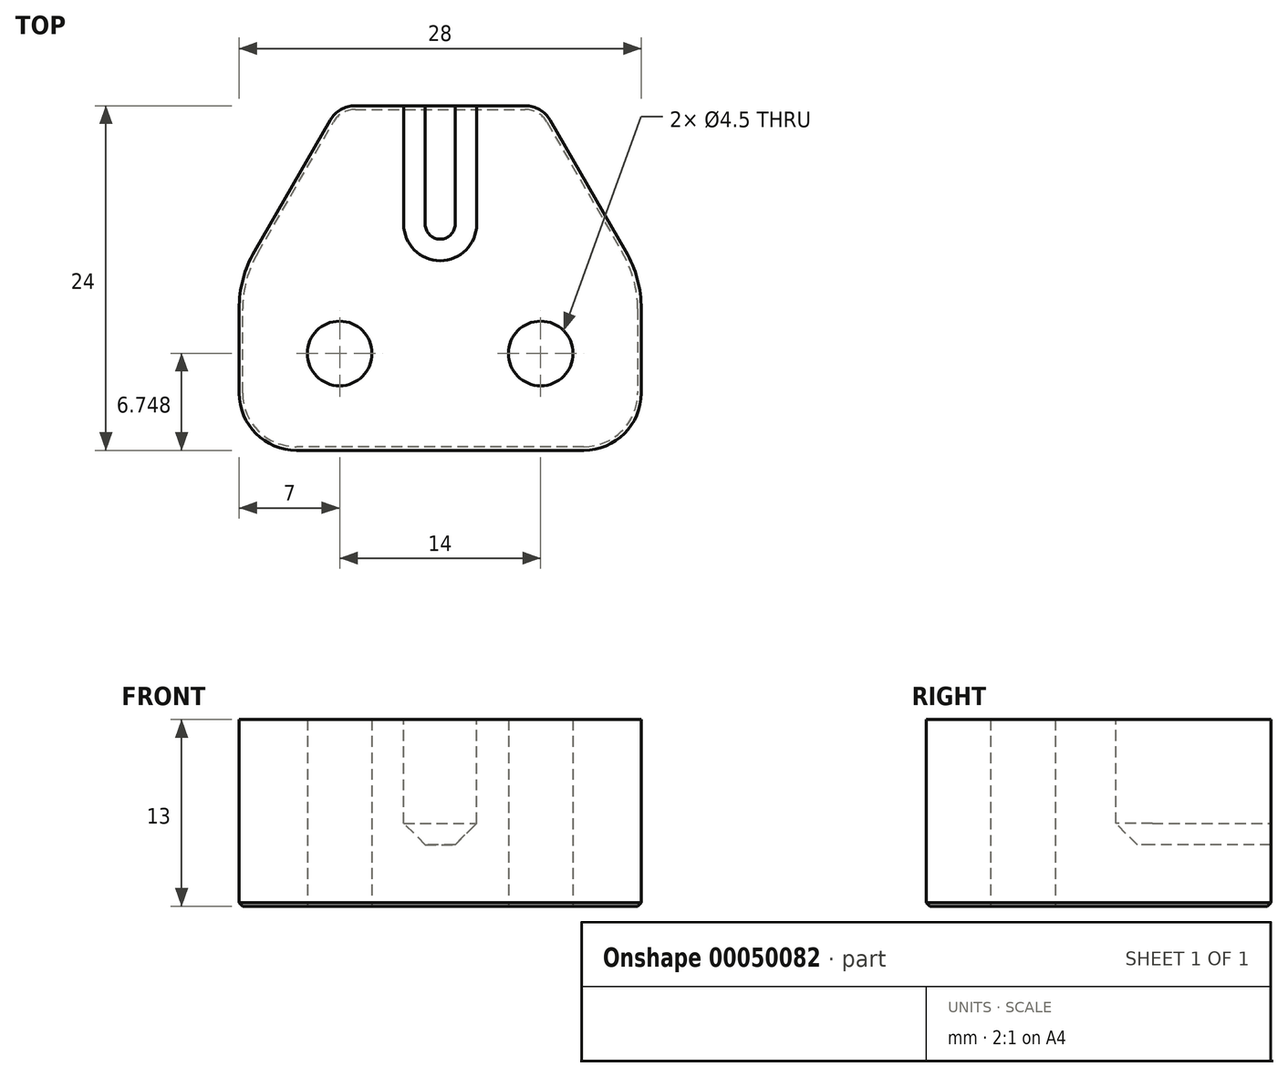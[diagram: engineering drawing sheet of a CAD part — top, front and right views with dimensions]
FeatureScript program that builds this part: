
annotation { "Feature Type Name" : "Feature", "Feature Type Description" : "" }
export const myFeature = defineFeature(function(context is Context, id is Id, definition is map)
    precondition{}
    {
        {
            var Q0;
            Q0=qCreatedBy(makeId("Top.planeOp"),FACE);
            var sketch = newSketch(context, id + "F0", { "sketchPlane" : qUnion([Q0])});
            skLineSegment(sketch, "E0", {"start": v(14, 2.75) * mm, "end": v(14, 14.75) * mm});
            skLineSegment(sketch, "E1", {"start": v(14, 14.75) * mm, "end": v(7.07, 26.75) * mm});
            skLineSegment(sketch, "E2", {"start": v(7.07, 26.75) * mm, "end": v(0, 26.75) * mm});
            skLineSegment(sketch, "E3", {"start": v(14, 2.75) * mm, "end": v(0, 2.75) * mm});
            skLineSegment(sketch, "E4.MirrorCS", {"start": v(-14, 2.75) * mm, "end": v(0, 2.75) * mm});
            skLineSegment(sketch, "E5.MirrorCS", {"start": v(-14, 2.75) * mm, "end": v(-14, 14.75) * mm});
            skLineSegment(sketch, "E6.MirrorCS", {"start": v(-7.07, 26.75) * mm, "end": v(0, 26.75) * mm});
            skLineSegment(sketch, "E7.MirrorCS", {"start": v(-14, 14.75) * mm, "end": v(-7.07, 26.75) * mm});
            skSolve(sketch);
        }
        {
            var Q0;
            Q0 = qSketchRegion(id + "F0", true);
            extrude(context, id + "F1", {"entities" : qUnion([Q0]), "depth" : 13 * mm});
        }
        {
            var Q0;
            Q0=makeQuery(id+"F1.opExtrude","SWEPT_EDGE",EDGE,{"disambiguationData":[OSD([sQuery(id+"F0.wireOp",EDGE,"E5.MirrorCS"),sQuery(id+"F0.wireOp",EDGE,"E7.MirrorCS")])]});
            var Q1;
            Q1=makeQuery(id+"F1.opExtrude","SWEPT_EDGE",EDGE,{"disambiguationData":[OSD([sQuery(id+"F0.wireOp",EDGE,"E0"),sQuery(id+"F0.wireOp",EDGE,"E1")])]});
            fillet(context, id + "F2", {"entities" : qUnion([Q0, Q1]), "radius" : 8 * mm, "tangentPropagation" : true, "allowEdgeOverflow" : false});
        }
        {
            var Q0;
            Q0=makeQuery(id+"F1.opExtrude","SWEPT_EDGE",EDGE,{"disambiguationData":[OSD([sQuery(id+"F0.wireOp",EDGE,"E6.MirrorCS"),sQuery(id+"F0.wireOp",EDGE,"E7.MirrorCS")])]});
            var Q1;
            Q1=makeQuery(id+"F1.opExtrude","SWEPT_EDGE",EDGE,{"disambiguationData":[OSD([sQuery(id+"F0.wireOp",EDGE,"E1"),sQuery(id+"F0.wireOp",EDGE,"E2")])]});
            fillet(context, id + "F3", {"entities" : qUnion([Q0, Q1]), "radius" : 2 * mm, "tangentPropagation" : true, "allowEdgeOverflow" : false});
        }
        {
            var Q0;
            Q0=makeQuery(id+"F1.opExtrude","CAP_FACE",FACE,{"disambiguationData":[OSD([sQuery(id+"F0.wireOp",EDGE,"E0"),sQuery(id+"F0.wireOp",EDGE,"E1"),sQuery(id+"F0.wireOp",EDGE,"E2"),sQuery(id+"F0.wireOp",EDGE,"E3"),sQuery(id+"F0.wireOp",EDGE,"E4.MirrorCS"),sQuery(id+"F0.wireOp",EDGE,"E5.MirrorCS"),sQuery(id+"F0.wireOp",EDGE,"E6.MirrorCS"),sQuery(id+"F0.wireOp",EDGE,"E7.MirrorCS")])],"isStart":false});
            var sketch = newSketch(context, id + "F4", { "sketchPlane" : qUnion([Q0])});
            skArc(sketch, "E8", {"start": v(-2.54, 18.5) * mm, "mid": v(0, 15.96) * mm, "end": v(2.54, 18.5) * mm});
            skLineSegment(sketch, "E9", {"start": v(-2.54, 18.5) * mm, "end": v(-2.54, 26.75) * mm});
            skLineSegment(sketch, "E10", {"start": v(2.54, 18.5) * mm, "end": v(2.54, 26.75) * mm});
            skLineSegment(sketch, "E11", {"start": v(2.54, 26.75) * mm, "end": v(-2.54, 26.75) * mm});
            skSolve(sketch);
        }
        {
            var Q0;
            Q0 = qSketchRegion(id + "F4", true);
            extrude(context, id + "F5", {"entities" : qUnion([Q0]), "operationType" : NewBodyOperationType.REMOVE, "oppositeDirection" : true, "depth" : (11 / 32 * 25.4) * mm, "offsetDistance" : 25 * mm});
        }
        {
            var Q0;
            Q0=makeQuery(id+"F1.opExtrude","CAP_FACE",FACE,{"disambiguationData":[OSD([sQuery(id+"F0.wireOp",EDGE,"E0"),sQuery(id+"F0.wireOp",EDGE,"E1"),sQuery(id+"F0.wireOp",EDGE,"E2"),sQuery(id+"F0.wireOp",EDGE,"E3"),sQuery(id+"F0.wireOp",EDGE,"E4.MirrorCS"),sQuery(id+"F0.wireOp",EDGE,"E5.MirrorCS"),sQuery(id+"F0.wireOp",EDGE,"E6.MirrorCS"),sQuery(id+"F0.wireOp",EDGE,"E7.MirrorCS")])],"isStart":true});
            var sketch = newSketch(context, id + "F6", { "sketchPlane" : qUnion([Q0])});
            skCircle(sketch, "E12", {"center": v(-7, -9.5) * mm, "radius": 2.25 * mm});
            skCircle(sketch, "E13.MirrorC", {"center": v(7, -9.5) * mm, "radius": 2.25 * mm});
            skSolve(sketch);
        }
        {
            var Q0;
            Q0 = qSketchRegion(id + "F6", true);
            extrude(context, id + "F7", {"entities" : qUnion([Q0]), "operationType" : NewBodyOperationType.REMOVE, "endBound" : BoundingType.THROUGH_ALL, "oppositeDirection" : true, "depth" : 25 * mm});
        }
        {
            var Q0;
            Q0=makeQuery(id+"F1.opExtrude","SWEPT_EDGE",EDGE,{"disambiguationData":[OSD([sQuery(id+"F0.wireOp",EDGE,"E4.MirrorCS"),sQuery(id+"F0.wireOp",EDGE,"E5.MirrorCS")])]});
            var Q1;
            Q1=makeQuery(id+"F1.opExtrude","SWEPT_EDGE",EDGE,{"disambiguationData":[OSD([sQuery(id+"F0.wireOp",EDGE,"E0"),sQuery(id+"F0.wireOp",EDGE,"E3")])]});
            fillet(context, id + "F8", {"entities" : qUnion([Q0, Q1]), "radius" : 4 * mm, "tangentPropagation" : true, "allowEdgeOverflow" : false});
        }
        {
            var Q0;
            Q0=makeQuery(id+"F5.boolean.opBoolean","COPY",EDGE,{"derivedFrom":makeQuery(id+"F5.opExtrude","CAP_EDGE",EDGE,{"disambiguationData":[OSD([sQuery(id+"F4.wireOp",EDGE,"E8")])],"isStart":false})});
            chamfer(context, id + "F9", {"entities" : qUnion([Q0]), "width" : 1.5 * mm, "tangentPropagation" : true});
        }
        {
            var Q0;
            Q0=makeQuery(id+"F7.boolean.opBoolean","COPY",EDGE,{"derivedFrom":makeQuery(id+"F7.opExtrude","CAP_EDGE",EDGE,{"disambiguationData":[OSD([sQuery(id+"F6.wireOp",EDGE,"E13.MirrorC")])],"isStart":true})});
            var Q1;
            Q1=makeQuery(id+"F7.boolean.opBoolean","COPY",EDGE,{"derivedFrom":makeQuery(id+"F7.opExtrude","CAP_EDGE",EDGE,{"disambiguationData":[OSD([sQuery(id+"F6.wireOp",EDGE,"E12")])],"isStart":true})});
            var Q2;
            Q2=makeQuery(id+"F1.opExtrude","CAP_EDGE",EDGE,{"disambiguationData":[OSD([sQuery(id+"F0.wireOp",EDGE,"E1")])],"isStart":true});
            chamfer(context, id + "F10", {"entities" : qUnion([Q0, Q1, Q2]), "width" : .25 * mm, "tangentPropagation" : true});
        }
    });
